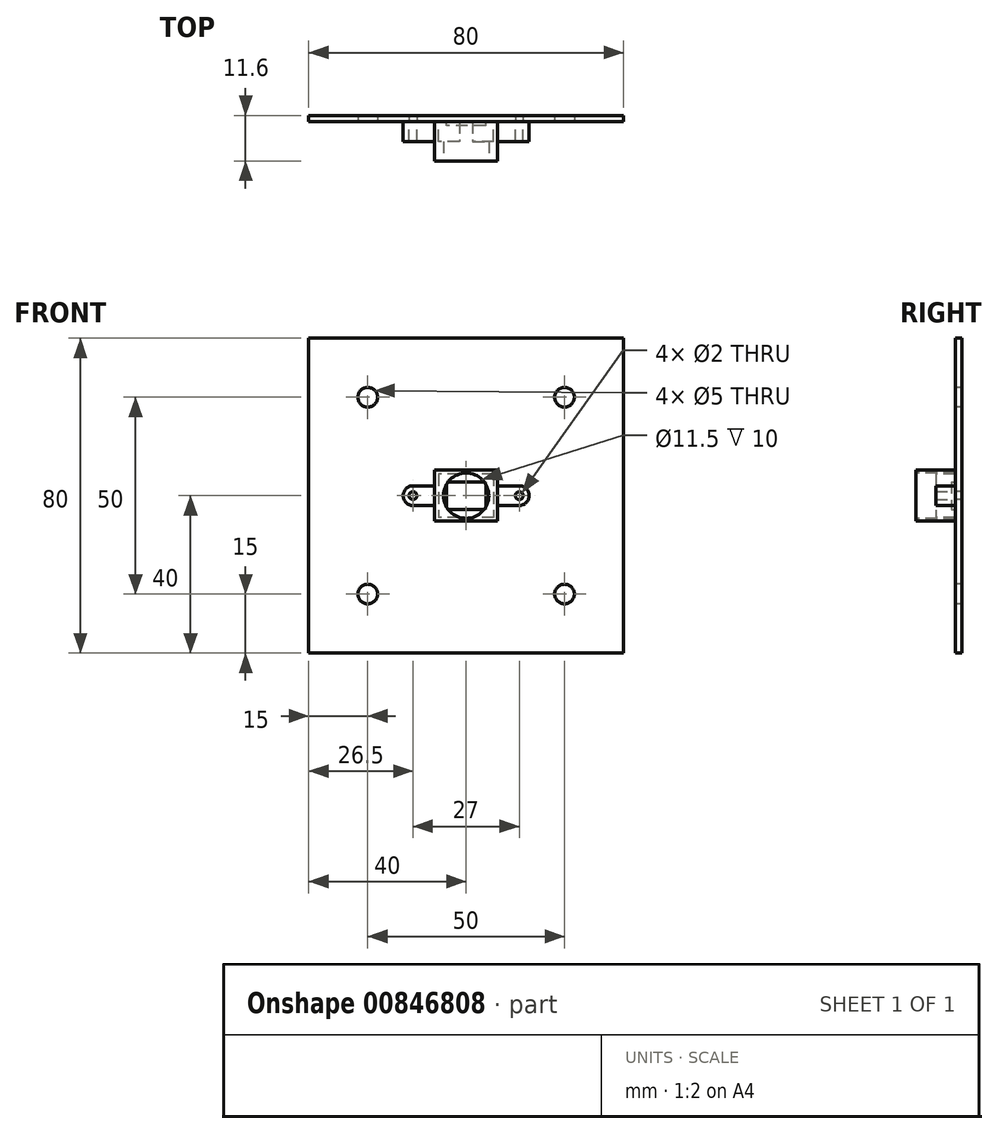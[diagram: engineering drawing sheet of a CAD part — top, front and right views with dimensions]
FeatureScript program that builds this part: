
annotation { "Feature Type Name" : "Feature", "Feature Type Description" : "" }
export const myFeature = defineFeature(function(context is Context, id is Id, definition is map)
    precondition{}
    {
        {
            var Q0;
            Q0=qCreatedBy(makeId("Front.planeOp"),FACE);
            var sketch = newSketch(context, id + "F0", { "sketchPlane" : qUnion([Q0])});
            skLineSegment(sketch, "E0.bottom", {"start": v(40, 40) * mm, "end": v(-40, 40) * mm});
            skLineSegment(sketch, "E0.top", {"start": v(40, -40) * mm, "end": v(-40, -40) * mm});
            skLineSegment(sketch, "E0.left", {"start": v(40, 40) * mm, "end": v(40, -40) * mm});
            skLineSegment(sketch, "E0.right", {"start": v(-40, 40) * mm, "end": v(-40, -40) * mm});
            skPoint(sketch, "E0.middle", {"position": v(0, 0) * mm});
            skLineSegment(sketch, "E1.bottom", {"start": v(25, 25) * mm, "end": v(-25, 25) * mm, "construction": true});
            skLineSegment(sketch, "E1.top", {"start": v(25, -25) * mm, "end": v(-25, -25) * mm, "construction": true});
            skLineSegment(sketch, "E1.left", {"start": v(25, 25) * mm, "end": v(25, -25) * mm, "construction": true});
            skLineSegment(sketch, "E1.right", {"start": v(-25, 25) * mm, "end": v(-25, -25) * mm, "construction": true});
            skCircle(sketch, "E2", {"center": v(25, 25) * mm, "radius": 2.5 * mm});
            skCircle(sketch, "E3", {"center": v(25, -25) * mm, "radius": 2.5 * mm});
            skCircle(sketch, "E4", {"center": v(-25, -25) * mm, "radius": 2.5 * mm});
            skCircle(sketch, "E5", {"center": v(-25, 25) * mm, "radius": 2.5 * mm});
            skLineSegment(sketch, "E6", {"start": v(-49.44, 0) * mm, "end": v(59.91, 0) * mm, "construction": true});
            skLineSegment(sketch, "E7", {"start": v(0, 49.46) * mm, "end": v(0, -57.48) * mm, "construction": true});
            skPoint(sketch, "E7.endSnap0", {"position": v(0, -25) * mm});
            skCircle(sketch, "E8", {"center": v(13.5, 0) * mm, "radius": 1 * mm});
            skCircle(sketch, "E9", {"center": v(-13.5, 0) * mm, "radius": 1 * mm});
            skLineSegment(sketch, "E10.bottom", {"start": v(5, 3.5) * mm, "end": v(-5, 3.5) * mm});
            skLineSegment(sketch, "E10.top", {"start": v(5, -3.5) * mm, "end": v(-5, -3.5) * mm});
            skLineSegment(sketch, "E10.left", {"start": v(5, 3.5) * mm, "end": v(5, -3.5) * mm});
            skLineSegment(sketch, "E10.right", {"start": v(-5, 3.5) * mm, "end": v(-5, -3.5) * mm});
            skSolve(sketch);
        }
        {
            var Q0;
            Q0=makeQuery(id+"F0.imprint","IMPRINT",FACE,{"disambiguationData":[TD([[makeQuery(id+"F0.imprint","IMPRINT",EDGE,{"derivedFrom":sQuery(id+"F0.wireOp",EDGE,"E0.bottom")}),1.0]])]});
            var Q1;
            Q1=makeQuery(id+"F0.imprint","IMPRINT",FACE,{"disambiguationData":[TD([[makeQuery(id+"F0.imprint","IMPRINT",EDGE,{"derivedFrom":sQuery(id+"F0.wireOp",EDGE,"E10.bottom")}),1.0]])]});
            extrude(context, id + "F1", {"entities" : qUnion([Q0, Q1]), "oppositeDirection" : true, "depth" : 1.6 * mm, "offsetDistance" : 25 * mm});
        }
        {
            var Q0;
            Q0=makeQuery(id+"F0.imprint","IMPRINT",FACE,{"disambiguationData":[TD([[makeQuery(id+"F0.imprint","IMPRINT",EDGE,{"derivedFrom":sQuery(id+"F0.wireOp",EDGE,"E10.bottom")}),1.0]])]});
            extrude(context, id + "F2", {"entities" : qUnion([Q0]), "depth" : 1 * mm, "offsetDistance" : 25 * mm});
        }
        {
            var Q0;
            Q0=makeQuery(id+"F1.opExtrude","CAP_FACE",FACE,{"disambiguationData":[OSD([sQuery(id+"F0.wireOp",EDGE,"E0.bottom"),sQuery(id+"F0.wireOp",EDGE,"E0.top"),sQuery(id+"F0.wireOp",EDGE,"E0.left"),sQuery(id+"F0.wireOp",EDGE,"E0.right"),sQuery(id+"F0.wireOp",EDGE,"E2"),sQuery(id+"F0.wireOp",EDGE,"E3"),sQuery(id+"F0.wireOp",EDGE,"E4"),sQuery(id+"F0.wireOp",EDGE,"E5"),sQuery(id+"F0.wireOp",EDGE,"E8"),sQuery(id+"F0.wireOp",EDGE,"E9")])],"isStart":true});
            var sketch = newSketch(context, id + "F3", { "sketchPlane" : qUnion([Q0])});
            skArc(sketch, "E11", {"start": v(13.5, -2.5) * mm, "mid": v(16, 0) * mm, "end": v(13.5, 2.5) * mm});
            skArc(sketch, "E12", {"start": v(-13.5, 2.5) * mm, "mid": v(-16, 0) * mm, "end": v(-13.5, -2.5) * mm});
            skLineSegment(sketch, "E13.bottom", {"start": v(13.5, 2.5) * mm, "end": v(8, 2.5) * mm});
            skLineSegment(sketch, "E13.top", {"start": v(13.5, -2.5) * mm, "end": v(8, -2.5) * mm});
            skPoint(sketch, "E13.middle", {"position": v(0, 0) * mm});
            skLineSegment(sketch, "E14.bottom", {"start": v(7, 5.5) * mm, "end": v(-7, 5.5) * mm});
            skLineSegment(sketch, "E14.top", {"start": v(7, -5.5) * mm, "end": v(-7, -5.5) * mm});
            skLineSegment(sketch, "E14.left", {"start": v(7, 5.5) * mm, "end": v(7, -5.5) * mm});
            skLineSegment(sketch, "E14.right", {"start": v(-7, 5.5) * mm, "end": v(-7, -5.5) * mm});
            skLineSegment(sketch, "E15.bottom", {"start": v(8, 6.5) * mm, "end": v(-8, 6.5) * mm});
            skLineSegment(sketch, "E15.top", {"start": v(8, -6.5) * mm, "end": v(-8, -6.5) * mm});
            skLineSegment(sketch, "E15.left", {"start": v(8, 6.5) * mm, "end": v(8, 2.5) * mm});
            skLineSegment(sketch, "E15.right", {"start": v(-8, 6.5) * mm, "end": v(-8, 2.5) * mm});
            skLineSegment(sketch, "E16.trimOffspring", {"start": v(-8, 2.5) * mm, "end": v(-13.5, 2.5) * mm});
            skLineSegment(sketch, "E17.trimOffspring", {"start": v(-8, -2.5) * mm, "end": v(-13.5, -2.5) * mm});
            skLineSegment(sketch, "E18.trimOffspring", {"start": v(8, -2.5) * mm, "end": v(8, -6.5) * mm});
            skLineSegment(sketch, "E19.trimOffspring", {"start": v(-8, -2.5) * mm, "end": v(-8, -6.5) * mm});
            skSolve(sketch);
        }
        {
            var Q0;
            Q0=makeQuery(id+"F3.imprint","IMPRINT",FACE,{"disambiguationData":[TD([[makeQuery(id+"F3.imprint","IMPRINT",EDGE,{"derivedFrom":sQuery(id+"F3.wireOp",EDGE,"E11")}),1.0]])]});
            extrude(context, id + "F4", {"entities" : qUnion([Q0]), "depth" : 5 * mm, "offsetDistance" : 25 * mm});
        }
        {
            var Q0;
            Q0=makeQuery(id+"F4.opExtrude","CAP_FACE",FACE,{"disambiguationData":[OSD([sQuery(id+"F0.wireOp",EDGE,"E8"),sQuery(id+"F0.wireOp",EDGE,"E9"),sQuery(id+"F3.wireOp",EDGE,"E11"),sQuery(id+"F3.wireOp",EDGE,"E12"),sQuery(id+"F3.wireOp",EDGE,"E13.bottom"),sQuery(id+"F3.wireOp",EDGE,"E13.top"),sQuery(id+"F3.wireOp",EDGE,"E14.bottom"),sQuery(id+"F3.wireOp",EDGE,"E14.top"),sQuery(id+"F3.wireOp",EDGE,"E14.left"),sQuery(id+"F3.wireOp",EDGE,"E14.right"),sQuery(id+"F3.wireOp",EDGE,"E15.bottom"),sQuery(id+"F3.wireOp",EDGE,"E15.top"),sQuery(id+"F3.wireOp",EDGE,"E15.left"),sQuery(id+"F3.wireOp",EDGE,"E15.right")])],"isStart":false});
            var sketch = newSketch(context, id + "F5", { "sketchPlane" : qUnion([Q0])});
            skLineSegment(sketch, "E20.bottom", {"start": v(-8, 6.5) * mm, "end": v(8, 6.5) * mm});
            skLineSegment(sketch, "E20.top", {"start": v(-8, -6.5) * mm, "end": v(8, -6.5) * mm});
            skLineSegment(sketch, "E20.left", {"start": v(-8, 6.5) * mm, "end": v(-8, -6.5) * mm});
            skLineSegment(sketch, "E20.right", {"start": v(8, 6.5) * mm, "end": v(8, -6.5) * mm});
            skSolve(sketch);
        }
        {
            var Q0;
            {var subQ4=sQuery(id+"F5.wireOp",EDGE,"E20.bottom");Q0=makeQuery(id+"F5.imprint","IMPRINT",FACE,{"disambiguationData":[TD([[makeQuery(id+"F5.imprint","IMPRINT",EDGE,{"derivedFrom":subQ4}),1.0]])]});}
            var Q1;
            Q1=makeQuery(id+"F5.imprint","IMPRINT",FACE,{"disambiguationData":[TD([[makeQuery(id+"F5.imprint","IMPRINT",EDGE,{"derivedFrom":makeQuery(id+"F4.opExtrude","CAP_EDGE",EDGE,{"disambiguationData":[OSD([sQuery(id+"F3.wireOp",EDGE,"E14.bottom")])],"isStart":false})}),1.0]])]});
            extrude(context, id + "F6", {"entities" : qUnion([Q0, Q1]), "operationType" : NewBodyOperationType.ADD, "depth" : 5 * mm, "offsetDistance" : 25 * mm});
        }
        {
            var Q0;
            Q0=makeQuery(id+"F6.opExtrude","CAP_FACE",FACE,{"disambiguationData":[OSD([sQuery(id+"F5.wireOp",EDGE,"E20.bottom"),sQuery(id+"F5.wireOp",EDGE,"E20.top"),sQuery(id+"F5.wireOp",EDGE,"E20.left"),sQuery(id+"F5.wireOp",EDGE,"E20.right")])],"isStart":false});
            var sketch = newSketch(context, id + "F7", { "sketchPlane" : qUnion([Q0])});
            skLineSegment(sketch, "E21", {"start": v(-9, -7.5) * mm, "end": v(9, 7.5) * mm, "construction": true});
            skLineSegment(sketch, "E22", {"start": v(-9, 7.5) * mm, "end": v(9, -7.5) * mm, "construction": true});
            skPoint(sketch, "E23", {"position": v(0, 0) * mm});
            skSolve(sketch);
        }
        {
            var Q0;
            Q0=sQuery(id+"F7.wireOp",VERTEX,"E23");
            var Q1;
            Q1=makeQuery(id+"F4.opExtrude","SWEPT_BODY",BODY,{"disambiguationData":[OSD([sQuery(id+"F0.wireOp",EDGE,"E8"),sQuery(id+"F0.wireOp",EDGE,"E9"),sQuery(id+"F3.wireOp",EDGE,"E11"),sQuery(id+"F3.wireOp",EDGE,"E12"),sQuery(id+"F3.wireOp",EDGE,"E13.bottom"),sQuery(id+"F3.wireOp",EDGE,"E13.top"),sQuery(id+"F3.wireOp",EDGE,"E14.bottom"),sQuery(id+"F3.wireOp",EDGE,"E14.top"),sQuery(id+"F3.wireOp",EDGE,"E14.left"),sQuery(id+"F3.wireOp",EDGE,"E14.right"),sQuery(id+"F3.wireOp",EDGE,"E15.bottom"),sQuery(id+"F3.wireOp",EDGE,"E15.top"),sQuery(id+"F3.wireOp",EDGE,"E15.left"),sQuery(id+"F3.wireOp",EDGE,"E15.right")])]});
            hole(context, id + "F8", {"style" : HoleStyle.SIMPLE, "endStyle" : HoleEndStyle.THROUGH, "holeDiameter" : 11.5 * mm, "majorDiameter" : 5 * mm, "isTappedThrough" : true, "tappedDepth" : 12 * mm, "tapClearance" : 3, "locations" : qUnion([Q0]), "scope" : qUnion([Q1])});
        }
    });
